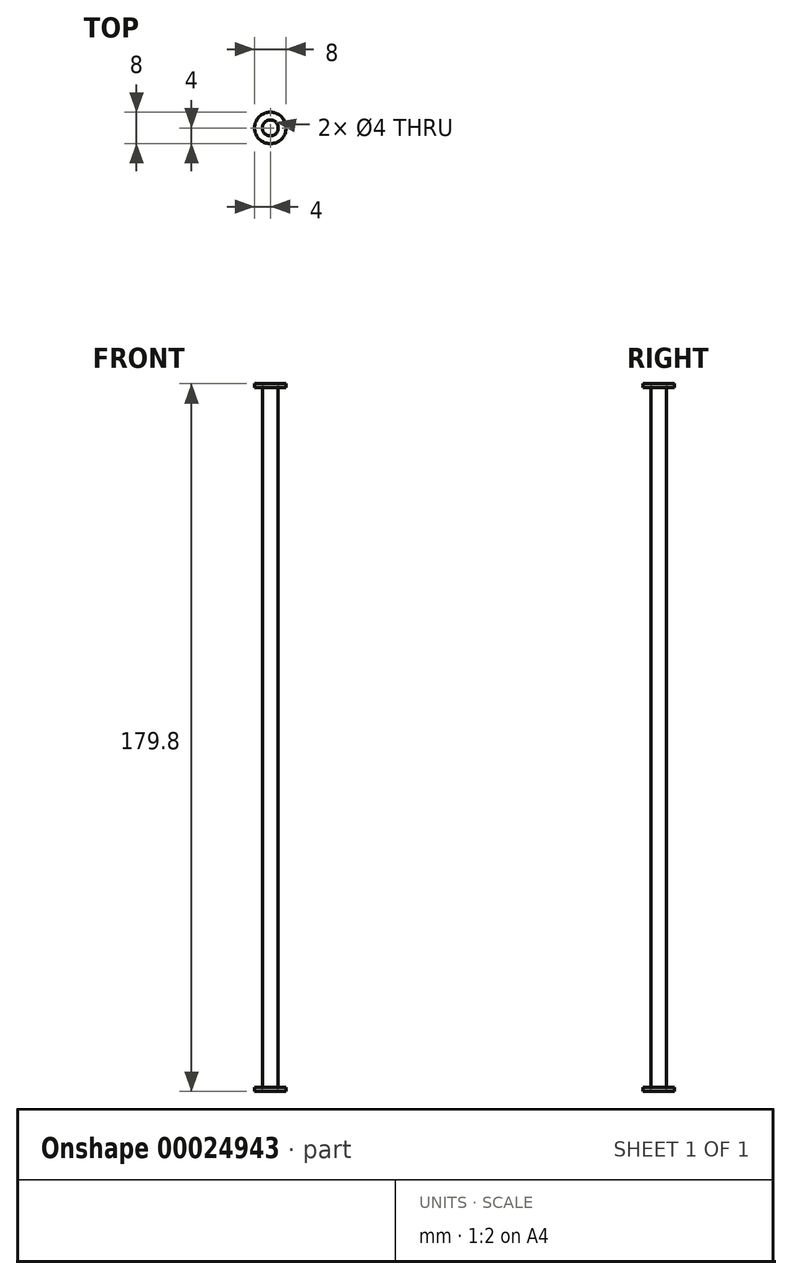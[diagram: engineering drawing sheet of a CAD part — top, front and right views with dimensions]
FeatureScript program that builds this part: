
annotation { "Feature Type Name" : "Feature", "Feature Type Description" : "" }
export const myFeature = defineFeature(function(context is Context, id is Id, definition is map)
    precondition{}
    {
        {
            var Q0;
            Q0=qCreatedBy(makeId("Top.planeOp"),FACE);
            var sketch = newSketch(context, id + "F0", { "sketchPlane" : qUnion([Q0])});
            skCircle(sketch, "E0", {"center": v(0, 0) * mm, "radius": 4 * mm});
            skCircle(sketch, "E1", {"center": v(0, 0) * mm, "radius": 2 * mm});
            skSolve(sketch);
        }
        {
            var Q0;
            Q0=makeQuery(id+"F0.imprint","IMPRINT",FACE,{"disambiguationData":[TD([[makeQuery(id+"F0.imprint","IMPRINT",EDGE,{"derivedFrom":sQuery(id+"F0.wireOp",EDGE,"E0")}),1.0]])]});
            extrude(context, id + "F1", {"entities" : qUnion([Q0]), "oppositeDirection" : true, "depth" : 1 * mm});
        }
        {
            var Q0;
            Q0=makeQuery(id+"F0.imprint","IMPRINT",FACE,{"disambiguationData":[TD([[makeQuery(id+"F0.imprint","IMPRINT",EDGE,{"derivedFrom":sQuery(id+"F0.wireOp",EDGE,"E1")}),1.0]])]});
            extrude(context, id + "F2", {"entities" : qUnion([Q0]), "operationType" : NewBodyOperationType.ADD, "depth" : 177.8 * mm});
        }
        {
            var Q0;
            Q0=makeQuery(id+"F2.opExtrude","CAP_FACE",FACE,{"disambiguationData":[OSD([sQuery(id+"F0.wireOp",EDGE,"E1")])],"isStart":false});
            var sketch = newSketch(context, id + "F3", { "sketchPlane" : qUnion([Q0])});
            skCircle(sketch, "E2", {"center": v(0, 0) * mm, "radius": 4 * mm});
            skSolve(sketch);
        }
        {
            var Q0;
            Q0=makeQuery(id+"F3.imprint","IMPRINT",FACE,{"disambiguationData":[TD([[makeQuery(id+"F3.imprint","IMPRINT",EDGE,{"derivedFrom":sQuery(id+"F3.wireOp",EDGE,"E2")}),1.0]])]});
            extrude(context, id + "F4", {"entities" : qUnion([Q0]), "depth" : 1 * mm});
        }
    });
